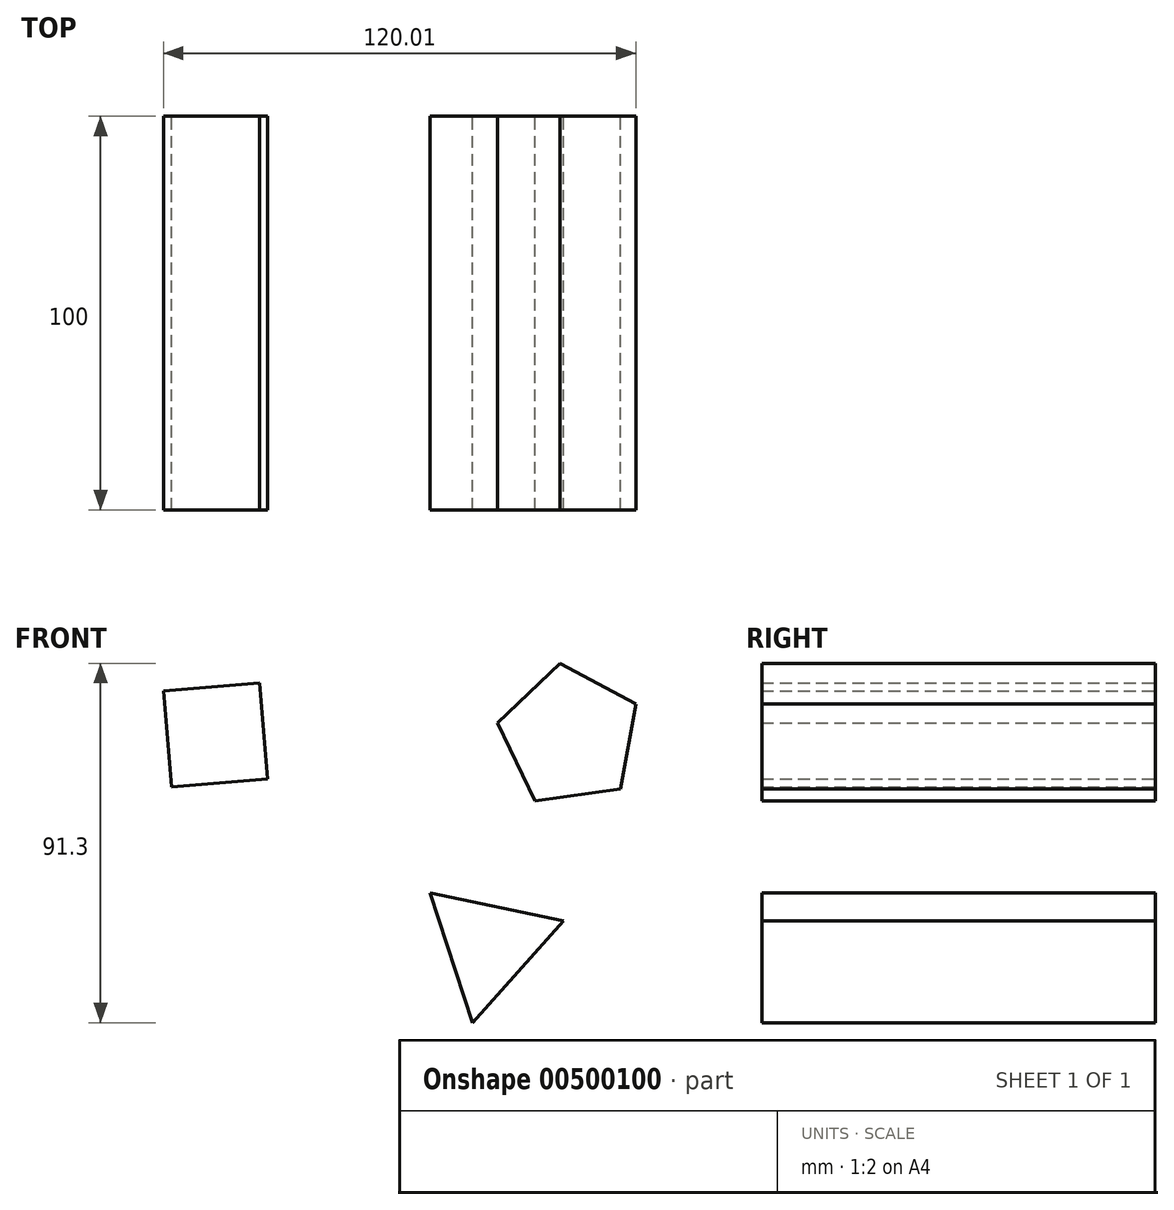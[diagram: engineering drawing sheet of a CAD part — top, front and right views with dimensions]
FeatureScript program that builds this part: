
annotation { "Feature Type Name" : "Feature", "Feature Type Description" : "" }
export const myFeature = defineFeature(function(context is Context, id is Id, definition is map)
    precondition{}
    {
        {
            var Q0;
            Q0=qCreatedBy(makeId("Front.planeOp"),FACE);
            var sketch = newSketch(context, id + "F0", { "sketchPlane" : qUnion([Q0])});
            skCircle(sketch, "E0.cCircle", {"center": v(0, 0) * mm, "radius": 20.01 * mm, "construction": true});
            skLineSegment(sketch, "E0.0", {"start": v(-14.92, 13.34) * mm, "end": v(19.01, 6.25) * mm});
            skLineSegment(sketch, "E0.1", {"start": v(19.01, 6.25) * mm, "end": v(-4.1, -19.59) * mm});
            skLineSegment(sketch, "E0.2", {"start": v(-4.1, -19.59) * mm, "end": v(-14.92, 13.34) * mm});
            skSolve(sketch);
        }
        {
            var Q0;
            Q0=makeQuery(id+"F0.imprint","IMPRINT",FACE,{"disambiguationData":[TD([[makeQuery(id+"F0.imprint","IMPRINT",EDGE,{"derivedFrom":sQuery(id+"F0.wireOp",EDGE,"E0.0")}),-1.0]])]});
            extrude(context, id + "F1", {"entities" : qUnion([Q0]), "depth" : 100 * mm});
        }
        {
            var Q0;
            Q0=qCreatedBy(makeId("Front.planeOp"),FACE);
            var sketch = newSketch(context, id + "F2", { "sketchPlane" : qUnion([Q0])});
            skCircle(sketch, "E1.cCircle", {"center": v(-69.43, 53.5) * mm, "radius": 17.3 * mm, "construction": true});
            skLineSegment(sketch, "E1.0", {"start": v(-56.23, 42.32) * mm, "end": v(-80.61, 40.3) * mm});
            skLineSegment(sketch, "E1.1", {"start": v(-80.61, 40.3) * mm, "end": v(-82.62, 64.7) * mm});
            skLineSegment(sketch, "E1.2", {"start": v(-82.62, 64.7) * mm, "end": v(-58.24, 66.7) * mm});
            skLineSegment(sketch, "E1.3", {"start": v(-58.24, 66.7) * mm, "end": v(-56.23, 42.32) * mm});
            skSolve(sketch);
        }
        {
            var Q0;
            Q0=makeQuery(id+"F2.imprint","IMPRINT",FACE,{"disambiguationData":[TD([[makeQuery(id+"F2.imprint","IMPRINT",EDGE,{"derivedFrom":sQuery(id+"F2.wireOp",EDGE,"E1.0")}),-1.0]])]});
            extrude(context, id + "F3", {"entities" : qUnion([Q0]), "depth" : 100 * mm});
        }
        {
            var Q0;
            Q0=qCreatedBy(makeId("Front.planeOp"),FACE);
            var sketch = newSketch(context, id + "F4", { "sketchPlane" : qUnion([Q0])});
            skCircle(sketch, "E2.cCircle", {"center": v(20.57, 53.22) * mm, "radius": 18.67 * mm, "construction": true});
            skLineSegment(sketch, "E2.0", {"start": v(33.48, 39.73) * mm, "end": v(11.74, 36.77) * mm});
            skLineSegment(sketch, "E2.1", {"start": v(11.74, 36.77) * mm, "end": v(2.2, 56.54) * mm});
            skLineSegment(sketch, "E2.2", {"start": v(2.2, 56.54) * mm, "end": v(18.05, 71.71) * mm});
            skLineSegment(sketch, "E2.3", {"start": v(18.05, 71.71) * mm, "end": v(37.39, 61.33) * mm});
            skLineSegment(sketch, "E2.4", {"start": v(37.39, 61.33) * mm, "end": v(33.48, 39.73) * mm});
            skSolve(sketch);
        }
        {
            var Q0;
            Q0=makeQuery(id+"F4.imprint","IMPRINT",FACE,{"disambiguationData":[TD([[makeQuery(id+"F4.imprint","IMPRINT",EDGE,{"derivedFrom":sQuery(id+"F4.wireOp",EDGE,"E2.0")}),-1.0]])]});
            extrude(context, id + "F5", {"entities" : qUnion([Q0]), "depth" : 100 * mm});
        }
    });
